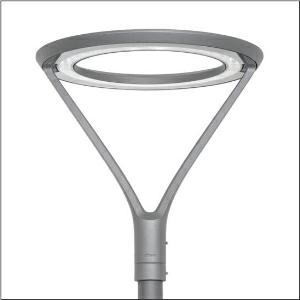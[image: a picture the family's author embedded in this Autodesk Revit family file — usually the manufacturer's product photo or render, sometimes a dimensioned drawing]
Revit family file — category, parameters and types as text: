
# Revit family: dl_r__20___st1_2a_5xa512832a008_56d6
name_source: partatom
category: Lighting Fixtures
units: mm (PartAtom-declared; Revit-internal decimal feet)

## family parameters
Cut with Voids When Loaded = No
Host = Face
Light Source = No
Part Type = Normal
Room Calculation Point = No
Round Connector Dimension = Use Diameter
Shared = No

## types (1)
- --- (1 x LED, 3020 lm, 30.4 W, 2200K)
    Apparent Load = 30 VA
    CIE Flux Codes = 32 72 97 100 100
    Color Rendering = 70
    Color Temperature = 2200K
    Default Elevation = 1800 mm
    Description = DL® 20, mast luminaire, primary light control with reflector, highly specular, primary optical cover: cover, of toughened safety glass of clear glass with excellent transmission level, light distribution: ST1.2a, light emission: direct distribution, primary light characteristic: asymmetric, installation type: post-top, LED, High Power LED, rated luminous flux: 3.020lm, luminous efficacy: 85lm/W, light colour: 722, colour temperature: 2200K, control gear: ECG Plus, control: flexible luminous flux parameterisation, time-dependent luminous flux control, constant luminous flux control, digital communication interface, power reduction, overheat protection, electronic power reduction, mains connection: 230..240V, 50/60Hz, connection cable pre-assembled, cable length: 5m, start of lifetime: 36W, end of service life: 36W, reduction: 17W, luminaire housing, upper part, of cast aluminium, powder-coated, Siteco® metallic grey (DB 702S), diameter: 690mm, height: 690mm, spigot size: 76mm (post-top), luminaire housing, of cast aluminium, powder-coated, Siteco® metallic grey (DB 702S), equipment: standard, protection rating (complete): IP66, insulation class (complete): insulation class II (safety insulation), certification: CE, ENEC, VDE, impact resistance: IK08, permissible operating ambient temperature: -25..+35°C, standard-compliant lighting for roads and squares, packaging unit: 1 piece

Light Distribution: ST1.2a
    Height = 690 mm
    Lamp = 1 x LED
    Lamp Light Flux = 3020 lm
    Lamp Power = 30.4 W
    Lamp count = 1
    Length = 690 mm
    Luminous efficacy = 99 lm/W
    Manufacturer = Siteco
    ModVariant = No
    Model = 5XA512832A008
    Number of Poles = 1
    OnlyDefault = Yes
    Power Factor = 1
    Product Name = DL® 20 | ST1.2a
    Product group = mast luminaire | pylon top
    ProductGroupID = 6100
    Protection Class = Protection class II
    Protection Degree = IP 66
    RLX_Detail_Level = 1
    RLX_Emergency_Light_Flux = 0 lm
    RLX_Emergency_Type = 0
    RLX_Emergency_Type_DB = No
    RlxData = <blob elided: 206505 chars, md5=d0b56ed5>
    Socket = socket
    Standby Power = 0 W
    System Light Flux = 3020 lm
    System Power = 30 W
    Type Comments = factory setting: luminous flux: 100 % | dim-lin: 254 | 412 mA
    Type Image = l_1006001.jpg
    URL = http://relux.com
    VarID = @adj_046549
    Voltage = 0 V
    Weight = 0.00 kg
    Width = 0 mm  [stored 0 ft]

note: [stored X ft] marks values corroborated as IEEE doubles in the binary element streams (Revit-internal decimal feet)

## geometry (parser evidence)
native form markers: Blend x4, Sweep x11
no freeform markers — native parametric forms only
